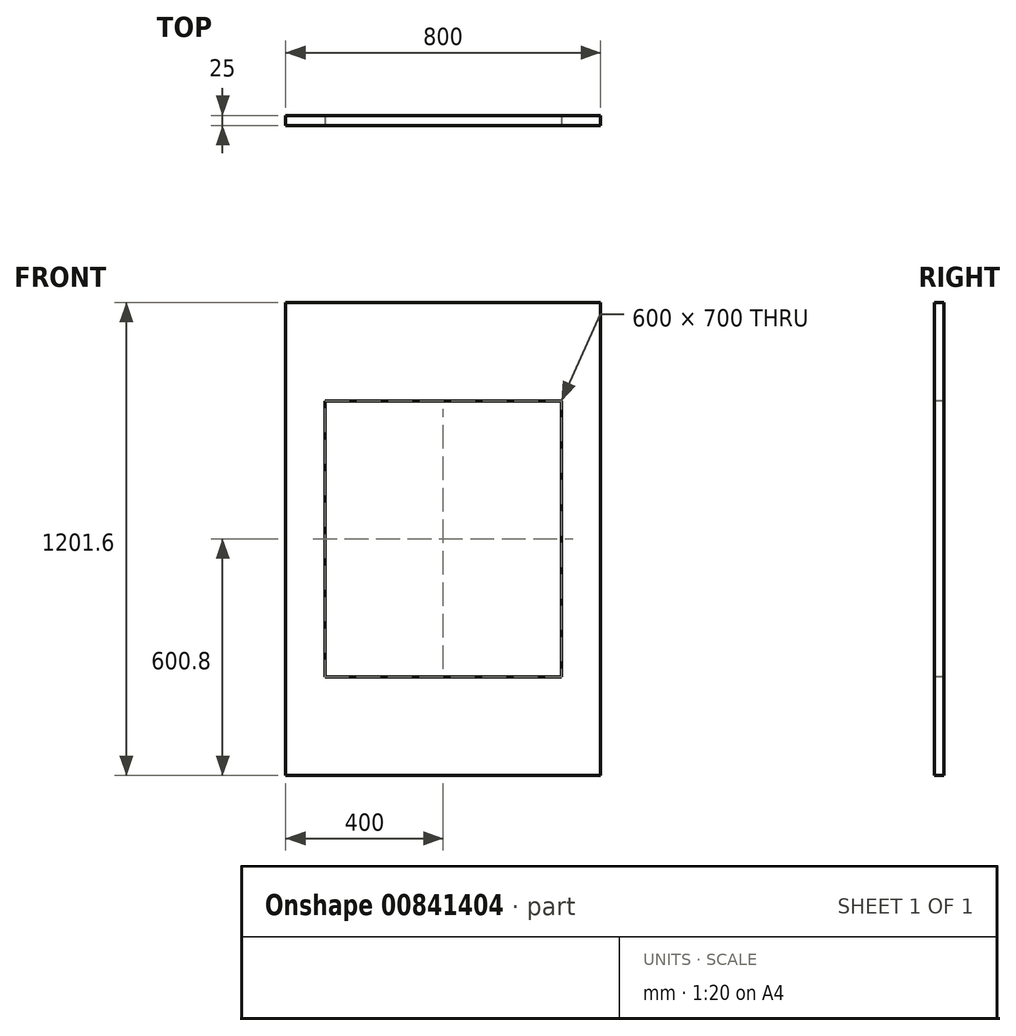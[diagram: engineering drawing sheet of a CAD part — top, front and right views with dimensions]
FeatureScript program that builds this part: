
annotation { "Feature Type Name" : "Feature", "Feature Type Description" : "" }
export const myFeature = defineFeature(function(context is Context, id is Id, definition is map)
    precondition{}
    {
        {
            var Q0;
            Q0=qCreatedBy(makeId("Front.planeOp"),FACE);
            var sketch = newSketch(context, id + "F0", { "sketchPlane" : qUnion([Q0])});
            skLineSegment(sketch, "E0.bottom", {"start": v(400, 600.8) * mm, "end": v(-400, 600.8) * mm});
            skLineSegment(sketch, "E0.top", {"start": v(400, -600.8) * mm, "end": v(-400, -600.8) * mm});
            skLineSegment(sketch, "E0.left", {"start": v(400, 600.8) * mm, "end": v(400, -600.8) * mm});
            skLineSegment(sketch, "E0.right", {"start": v(-400, 600.8) * mm, "end": v(-400, -600.8) * mm});
            skPoint(sketch, "E0.middle", {"position": v(0, 0) * mm});
            skSolve(sketch);
        }
        {
            var Q0;
            Q0=qSketchRegion(id+"F0",true);
            extrude(context, id + "F1", {"entities" : qUnion([Q0]), "depth" : 25 * mm, "offsetDistance" : 25 * mm});
        }
        {
            var Q0;
            Q0=makeQuery(id+"F1.opExtrude","CAP_FACE",FACE,{"disambiguationData":[OSD([sQuery(id+"F0.wireOp",EDGE,"E0.bottom"),sQuery(id+"F0.wireOp",EDGE,"E0.top"),sQuery(id+"F0.wireOp",EDGE,"E0.left"),sQuery(id+"F0.wireOp",EDGE,"E0.right")])],"isStart":false});
            var sketch = newSketch(context, id + "F2", { "sketchPlane" : qUnion([Q0])});
            skLineSegment(sketch, "E1.bottom", {"start": v(300, 350) * mm, "end": v(-300, 350) * mm});
            skLineSegment(sketch, "E1.top", {"start": v(300, -350) * mm, "end": v(-300, -350) * mm});
            skLineSegment(sketch, "E1.left", {"start": v(300, 350) * mm, "end": v(300, -350) * mm});
            skLineSegment(sketch, "E1.right", {"start": v(-300, 350) * mm, "end": v(-300, -350) * mm});
            skPoint(sketch, "E1.middle", {"position": v(0, 0) * mm});
            skSolve(sketch);
        }
        {
            var Q0;
            Q0 = qSketchRegion(id + "F2", true);
            extrude(context, id + "F3", {"entities" : qUnion([Q0]), "operationType" : NewBodyOperationType.REMOVE, "oppositeDirection" : true, "depth" : 608 * mm, "offsetDistance" : 25 * mm});
        }
    });
